MODEL slx_742cbf9d1e52
KIND model
CONFIG AbsTol = auto
CONFIG EnableMultiTasking = on
CONFIG FixedStep = 0.002
CONFIG MaxStep = auto
CONFIG MinStep = auto
CONFIG RelTol = 1e-3
CONFIG SampleTimeConstraint = Unconstrained
CONFIG Solver = ode2
CONFIG SolverName = ode2
CONFIG StartTime = 0.0
CONFIG StopTime = inf
WORKSPACE source: MAT-file member
WORKSPACE m = 1000
BLOCK [BusSelector] Bus Selector
  OutputAsBus = off
  OutputSignals = InitialState
  Ports = [1, 1]
BLOCK [BusSelector] Bus Selector1
  OutputAsBus = off
  OutputSignals = RequestSteeringAngle_rad,RequestLongForce_N,RequestThrottle_perc,RequestGear,RequestBrake_bar
  Ports = [1, 5]
BLOCK [ModelReference] Model
  ModelNameDialog = debug_conversion_debug.slx
  ModelReferenceVersion = 1.8
  Ports = [1, 1]
BLOCK [ModelReference] Model1
  ModelNameDialog = debug_conversion_debug_slow.slx
  ModelReferenceVersion = 1.8
  Ports = [1, 1]
BLOCK [ModelReference] Model2
  ModelNameDialog = convert_SimBus.slx
  ModelReferenceVersion = 1.821
  Ports = [3, 3]
BLOCK [ModelReference] PassengerVehicle
  ModelNameDialog = PassengerVehicle
  ModelReferenceVersion = 1.992
  Ports = [7, 4]
BLOCK [RateTransition] Rate Transition
BLOCK [RateTransition] Rate Transition1
BLOCK [RateTransition] Rate Transition10
BLOCK [RateTransition] Rate Transition2
BLOCK [RateTransition] Rate Transition3
BLOCK [RateTransition] Rate Transition4
BLOCK [RateTransition] Rate Transition5
BLOCK [RateTransition] Rate Transition6
BLOCK [RateTransition] Rate Transition7
BLOCK [RateTransition] Rate Transition8
BLOCK [RateTransition] Rate Transition9
BLOCK [Terminator] Terminator
BLOCK [Terminator] Terminator1
BLOCK [Terminator] Terminator2
BLOCK [Inport] in_ExternalDebug
  IconDisplay = Port number
  OutDataTypeStr = Bus: ExternalDebug
  Port = 4
BLOCK [Inport] in_MapReference
  IconDisplay = Port number
  OutDataTypeStr = Bus: MapReference
BLOCK [Inport] in_TrajectoryPlanning
  IconDisplay = Port number
  OutDataTypeStr = Bus: TrajectoryPlanning
  Port = 2
BLOCK [Inport] in_tpamapReference
  IconDisplay = Port number
  OutDataTypeStr = Bus: tpamapReference
  Port = 3
BLOCK [ModelReference] mvdc_vehicle_dynamics_control1
  ModelNameDialog = mvdc_vehicle_dynamics_control
  ModelReferenceVersion = 1.797
  Ports = [5, 10]
BLOCK [Outport] out_Debug
  IconDisplay = Port number
  Port = 3
BLOCK [Outport] out_Debug_Slow
  IconDisplay = Port number
  Port = 4
BLOCK [Outport] out_LiveVisualization_Send
  BusOutputAsStruct = on
  IconDisplay = Port number
  OutDataTypeStr = Bus: LiveVisualization
  Port = 7
  PortDimensions = 1
BLOCK [Outport] out_TUMModeControl
  IconDisplay = Port number
  OutDataTypeStr = Bus: TUMModeControl
  Port = 2
BLOCK [Outport] out_VehicleDynamicState
  IconDisplay = Port number
  OutDataTypeStr = Bus: VehicleDynamicState
BLOCK [Outport] out_tpa_mueest_rt
  IconDisplay = Port number
  OutDataTypeStr = Bus: mvdc_tpa_mueest_rt_Send
  Port = 5
BLOCK [Outport] out_tpa_vdcsignals
  IconDisplay = Port number
  OutDataTypeStr = Bus: mvdc_tpa_vdcsignals_Send
  Port = 6
ANNOTATION (root): Author: Alexander Wischnewski (<email>) Chair of Automatic Control at TU Munich Description: This model uses the control software provided in vehicle dynamics control and the nonlinear single track vehicle model with sensor models to simulate the example vehicle in closed loop. It is used to generate code for a python wrapper class.
LINE Bus Selector1:1 -> Rate Transition:1
LINE Bus Selector1:2 -> Rate Transition1:1
LINE Bus Selector1:3 -> Rate Transition8:1
LINE Bus Selector1:4 -> Rate Transition9:1
LINE Bus Selector1:5 -> Rate Transition10:1
LINE Bus Selector:1 -> PassengerVehicle:3
LINE Model1:1 -> out_Debug_Slow:1
LINE Model2:1 -> Rate Transition2:1
LINE Model2:2 -> Rate Transition6:1
LINE Model2:3 -> Rate Transition7:1
LINE Model:1 -> out_Debug:1
LINE PassengerVehicle:1 -> Rate Transition3:1
LINE PassengerVehicle:2 -> Rate Transition4:1
LINE PassengerVehicle:3 -> Rate Transition5:1
LINE PassengerVehicle:4 -> Terminator2:1
LINE Rate Transition10:1 -> PassengerVehicle:7
LINE Rate Transition1:1 -> PassengerVehicle:2
LINE Rate Transition2:1 -> mvdc_vehicle_dynamics_control1:3
LINE Rate Transition3:1 -> Model2:1
LINE Rate Transition4:1 -> Model2:2
LINE Rate Transition5:1 -> Model2:3
LINE Rate Transition6:1 -> mvdc_vehicle_dynamics_control1:4
LINE Rate Transition7:1 -> mvdc_vehicle_dynamics_control1:5
LINE Rate Transition8:1 -> PassengerVehicle:5
LINE Rate Transition9:1 -> PassengerVehicle:6
LINE Rate Transition:1 -> PassengerVehicle:1
LINE in_ExternalDebug:1 -> mvdc_vehicle_dynamics_control1:2
LINE in_MapReference:1 -> Bus Selector:1
LINE in_TrajectoryPlanning:1 -> mvdc_vehicle_dynamics_control1:1
LINE in_tpamapReference:1 -> PassengerVehicle:4
LINE mvdc_vehicle_dynamics_control1:1 -> Model:1
LINE mvdc_vehicle_dynamics_control1:10 -> out_LiveVisualization_Send:1
LINE mvdc_vehicle_dynamics_control1:2 -> out_VehicleDynamicState:1
LINE mvdc_vehicle_dynamics_control1:3 -> out_TUMModeControl:1
LINE mvdc_vehicle_dynamics_control1:4 -> Terminator:1
LINE mvdc_vehicle_dynamics_control1:5 -> Bus Selector1:1
LINE mvdc_vehicle_dynamics_control1:6 -> Terminator1:1
LINE mvdc_vehicle_dynamics_control1:7 -> out_tpa_mueest_rt:1
LINE mvdc_vehicle_dynamics_control1:8 -> out_tpa_vdcsignals:1
LINE mvdc_vehicle_dynamics_control1:9 -> Model1:1
